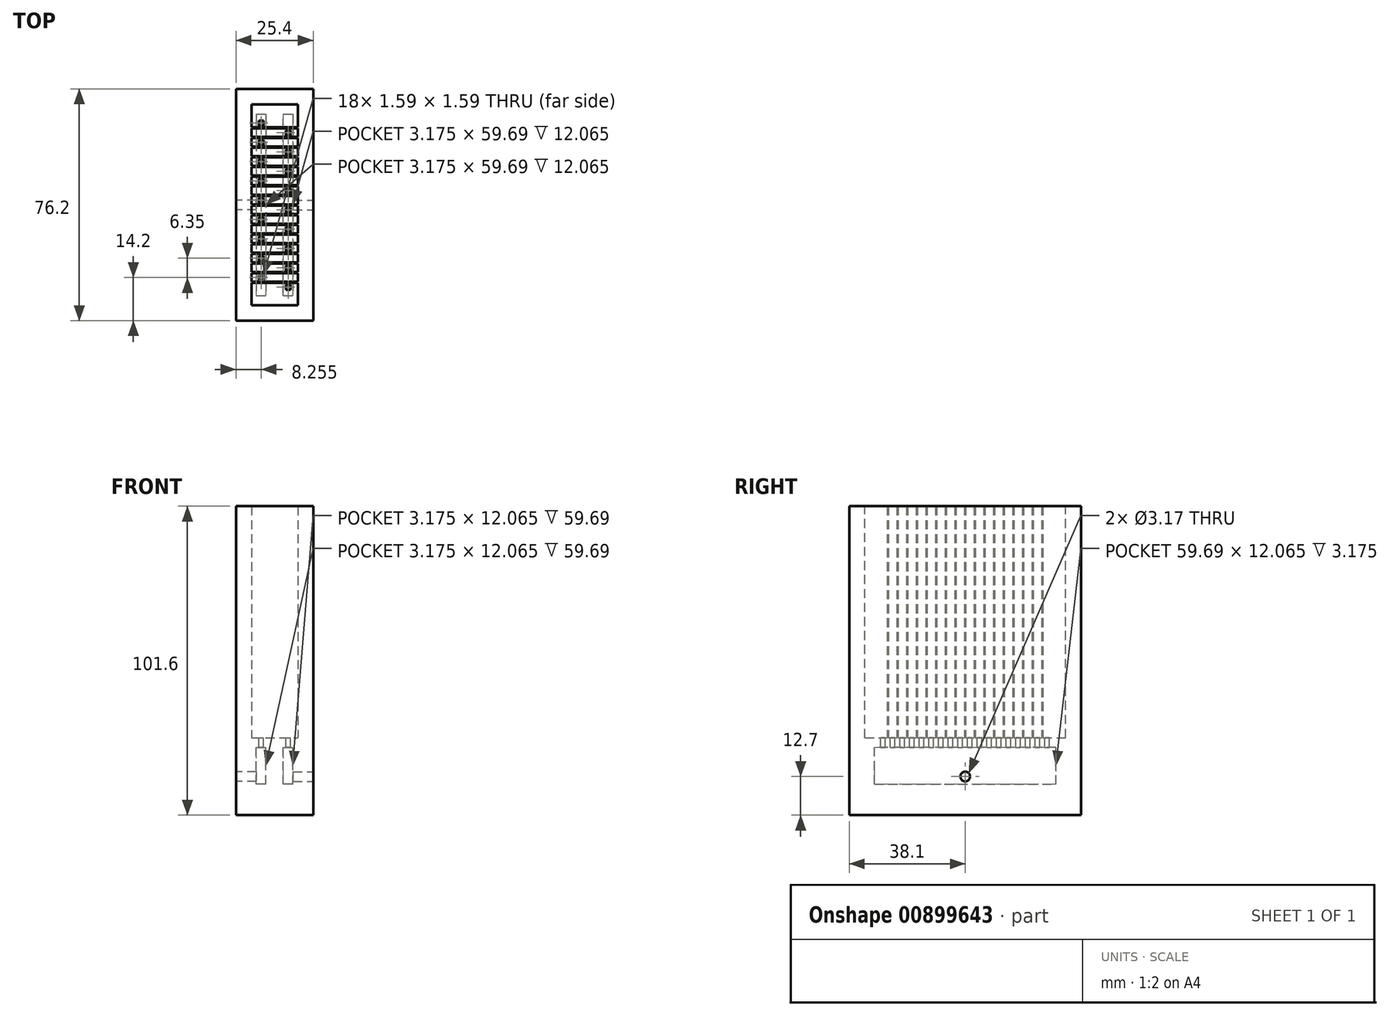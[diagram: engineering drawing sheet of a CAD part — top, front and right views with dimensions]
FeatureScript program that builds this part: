
annotation { "Feature Type Name" : "Feature", "Feature Type Description" : "" }
export const myFeature = defineFeature(function(context is Context, id is Id, definition is map)
    precondition{}
    {
        {
            var Q0;
            Q0=qCreatedBy(makeId("Top.planeOp"),FACE);
            var sketch = newSketch(context, id + "F0", { "sketchPlane" : qUnion([Q0])});
            skLineSegment(sketch, "E0.bottom", {"start": v(0, 0) * mm, "end": v(25.4, 0) * mm});
            skLineSegment(sketch, "E0.top", {"start": v(0, 76.2) * mm, "end": v(25.4, 76.2) * mm});
            skLineSegment(sketch, "E0.left", {"start": v(0, 0) * mm, "end": v(0, 76.2) * mm});
            skLineSegment(sketch, "E0.right", {"start": v(25.4, 0) * mm, "end": v(25.4, 76.2) * mm});
            skSolve(sketch);
        }
        {
            var Q0;
            Q0=makeQuery(id+"F0.imprint","IMPRINT",FACE,{"disambiguationData":[TD([[makeQuery(id+"F0.imprint","IMPRINT",EDGE,{"derivedFrom":sQuery(id+"F0.wireOp",EDGE,"E0.bottom")}),1.0]])]});
            extrude(context, id + "F1", {"entities" : qUnion([Q0]), "depth" : 101.6 * mm, "offsetDistance" : 25.4 * mm});
        }
        {
            var Q0;
            Q0=makeQuery(id+"F1.opExtrude","CAP_FACE",FACE,{"disambiguationData":[OSD([sQuery(id+"F0.wireOp",EDGE,"E0.bottom"),sQuery(id+"F0.wireOp",EDGE,"E0.top"),sQuery(id+"F0.wireOp",EDGE,"E0.left"),sQuery(id+"F0.wireOp",EDGE,"E0.right")])],"isStart":false});
            var sketch = newSketch(context, id + "F2", { "sketchPlane" : qUnion([Q0])});
            skLineSegment(sketch, "E1.bottom", {"start": v(5.08, 5.08) * mm, "end": v(20.32, 5.08) * mm});
            skLineSegment(sketch, "E1.top", {"start": v(5.08, 71.12) * mm, "end": v(20.32, 71.12) * mm});
            skLineSegment(sketch, "E1.left", {"start": v(5.08, 5.08) * mm, "end": v(5.08, 71.12) * mm});
            skLineSegment(sketch, "E1.right", {"start": v(20.32, 5.08) * mm, "end": v(20.32, 71.12) * mm});
            skSolve(sketch);
        }
        {
            var Q0;
            Q0=makeQuery(id+"F2.imprint","IMPRINT",FACE,{"disambiguationData":[TD([[makeQuery(id+"F2.imprint","IMPRINT",EDGE,{"derivedFrom":sQuery(id+"F2.wireOp",EDGE,"E1.bottom")}),1.0]])]});
            extrude(context, id + "F3", {"entities" : qUnion([Q0]), "operationType" : NewBodyOperationType.REMOVE, "oppositeDirection" : true, "depth" : 76.2 * mm, "offsetDistance" : 25.4 * mm});
        }
        {
            var Q0;
            Q0=makeQuery(id+"F1.opExtrude","SWEPT_FACE",FACE,{"disambiguationData":[OSD([sQuery(id+"F0.wireOp",EDGE,"E0.right")])]});
            var sketch = newSketch(context, id + "F4", { "sketchPlane" : qUnion([Q0])});
            skCircle(sketch, "E2", {"center": v(38.1, 12.7) * mm, "radius": 1.59 * mm});
            skSolve(sketch);
        }
        {
            var Q0;
            Q0=makeQuery(id+"F3.boolean.opBoolean","COPY",FACE,{"derivedFrom":makeQuery(id+"F3.opExtrude","CAP_FACE",FACE,{"disambiguationData":[OSD([sQuery(id+"F2.wireOp",EDGE,"E1.bottom"),sQuery(id+"F2.wireOp",EDGE,"E1.top"),sQuery(id+"F2.wireOp",EDGE,"E1.left"),sQuery(id+"F2.wireOp",EDGE,"E1.right")])],"isStart":false})});
            var sketch = newSketch(context, id + "F5", { "sketchPlane" : qUnion([Q0])});
            skLineSegment(sketch, "E3.bottom", {"start": v(15.56, 67.95) * mm, "end": v(18.73, 67.95) * mm});
            skLineSegment(sketch, "E3.top", {"start": v(15.56, 8.26) * mm, "end": v(18.73, 8.26) * mm});
            skLineSegment(sketch, "E3.left", {"start": v(15.56, 67.95) * mm, "end": v(15.56, 8.26) * mm});
            skLineSegment(sketch, "E3.right", {"start": v(18.73, 67.95) * mm, "end": v(18.73, 8.25) * mm});
            skLineSegment(sketch, "E4.bottom", {"start": v(6.67, 67.95) * mm, "end": v(9.84, 67.95) * mm});
            skLineSegment(sketch, "E4.top", {"start": v(6.67, 8.25) * mm, "end": v(9.84, 8.25) * mm});
            skLineSegment(sketch, "E4.left", {"start": v(6.67, 67.95) * mm, "end": v(6.67, 8.25) * mm});
            skLineSegment(sketch, "E4.right", {"start": v(9.84, 67.95) * mm, "end": v(9.84, 8.25) * mm});
            skSolve(sketch);
        }
        {
            var Q0;
            Q0 = qSketchRegion(id + "F5", true);
            extrude(context, id + "F6", {"entities" : qUnion([Q0]), "operationType" : NewBodyOperationType.REMOVE, "endBound" : BoundingType.UP_TO_NEXT, "oppositeDirection" : true, "depth" : 25.4 * mm, "hasOffset" : true, "offsetDistance" : 10.16 * mm, "hasSecondDirection" : true, "secondDirectionOppositeDirection" : false, "secondDirectionDepth" : -3.17 * mm});
        }
        {
            var Q0;
            Q0 = qSketchRegion(id + "F4", true);
            extrude(context, id + "F7", {"entities" : qUnion([Q0]), "operationType" : NewBodyOperationType.REMOVE, "endBound" : BoundingType.UP_TO_NEXT, "oppositeDirection" : true, "depth" : 25.4 * mm, "offsetDistance" : 25.4 * mm});
        }
        {
            var Q0;
            Q0=makeQuery(id+"F1.opExtrude","SWEPT_FACE",FACE,{"disambiguationData":[OSD([sQuery(id+"F0.wireOp",EDGE,"E0.left")])]});
            var sketch = newSketch(context, id + "F8", { "sketchPlane" : qUnion([Q0])});
            skCircle(sketch, "E5", {"center": v(-38.1, 12.7) * mm, "radius": 1.59 * mm});
            skSolve(sketch);
        }
        {
            var Q0;
            Q0 = qSketchRegion(id + "F8", true);
            extrude(context, id + "F9", {"entities" : qUnion([Q0]), "operationType" : NewBodyOperationType.REMOVE, "endBound" : BoundingType.UP_TO_NEXT, "oppositeDirection" : true, "depth" : 25.4 * mm, "offsetDistance" : 25.4 * mm});
        }
        {
            var Q0;
            Q0=makeQuery(id+"F3.boolean.opBoolean","COPY",FACE,{"derivedFrom":makeQuery(id+"F3.opExtrude","CAP_FACE",FACE,{"disambiguationData":[OSD([sQuery(id+"F2.wireOp",EDGE,"E1.bottom"),sQuery(id+"F2.wireOp",EDGE,"E1.top"),sQuery(id+"F2.wireOp",EDGE,"E1.left"),sQuery(id+"F2.wireOp",EDGE,"E1.right")])],"isStart":false})});
            var sketch = newSketch(context, id + "F10", { "sketchPlane" : qUnion([Q0])});
            skLineSegment(sketch, "E6.bottom", {"start": v(7.46, 65.8) * mm, "end": v(9.05, 65.8) * mm});
            skLineSegment(sketch, "E6.top", {"start": v(7.46, 64.2) * mm, "end": v(9.05, 64.2) * mm});
            skLineSegment(sketch, "E6.left", {"start": v(7.46, 65.8) * mm, "end": v(7.46, 64.2) * mm});
            skLineSegment(sketch, "E6.right", {"start": v(9.05, 65.8) * mm, "end": v(9.05, 64.2) * mm});
            skLineSegment(sketch, "E7.0.1.0", {"start": v(9.05, 59.44) * mm, "end": v(9.05, 57.86) * mm});
            skLineSegment(sketch, "E7.0.1.1", {"start": v(7.46, 59.44) * mm, "end": v(7.46, 57.86) * mm});
            skLineSegment(sketch, "E7.0.1.2", {"start": v(7.46, 57.86) * mm, "end": v(9.05, 57.86) * mm});
            skLineSegment(sketch, "E7.0.1.3", {"start": v(7.46, 59.44) * mm, "end": v(9.05, 59.44) * mm});
            skLineSegment(sketch, "E7.0.2.0", {"start": v(9.05, 53.1) * mm, "end": v(9.05, 51.5) * mm});
            skLineSegment(sketch, "E7.0.2.1", {"start": v(7.46, 53.1) * mm, "end": v(7.46, 51.5) * mm});
            skLineSegment(sketch, "E7.0.2.2", {"start": v(7.46, 51.5) * mm, "end": v(9.05, 51.5) * mm});
            skLineSegment(sketch, "E7.0.2.3", {"start": v(7.46, 53.1) * mm, "end": v(9.05, 53.1) * mm});
            skLineSegment(sketch, "E7.0.3.0", {"start": v(9.05, 46.74) * mm, "end": v(9.05, 45.16) * mm});
            skLineSegment(sketch, "E7.0.3.1", {"start": v(7.46, 46.74) * mm, "end": v(7.46, 45.16) * mm});
            skLineSegment(sketch, "E7.0.3.2", {"start": v(7.46, 45.16) * mm, "end": v(9.05, 45.16) * mm});
            skLineSegment(sketch, "E7.0.3.3", {"start": v(7.46, 46.74) * mm, "end": v(9.05, 46.74) * mm});
            skLineSegment(sketch, "E7.0.4.0", {"start": v(9.05, 40.4) * mm, "end": v(9.05, 38.8) * mm});
            skLineSegment(sketch, "E7.0.4.1", {"start": v(7.46, 40.4) * mm, "end": v(7.46, 38.8) * mm});
            skLineSegment(sketch, "E7.0.4.2", {"start": v(7.46, 38.8) * mm, "end": v(9.05, 38.8) * mm});
            skLineSegment(sketch, "E7.0.4.3", {"start": v(7.46, 40.4) * mm, "end": v(9.05, 40.4) * mm});
            skLineSegment(sketch, "E7.0.5.0", {"start": v(9.05, 34.04) * mm, "end": v(9.05, 32.46) * mm});
            skLineSegment(sketch, "E7.0.5.1", {"start": v(7.46, 34.04) * mm, "end": v(7.46, 32.46) * mm});
            skLineSegment(sketch, "E7.0.5.2", {"start": v(7.46, 32.46) * mm, "end": v(9.05, 32.46) * mm});
            skLineSegment(sketch, "E7.0.5.3", {"start": v(7.46, 34.04) * mm, "end": v(9.05, 34.04) * mm});
            skLineSegment(sketch, "E7.0.6.0", {"start": v(9.05, 27.7) * mm, "end": v(9.05, 26.1) * mm});
            skLineSegment(sketch, "E7.0.6.1", {"start": v(7.46, 27.7) * mm, "end": v(7.46, 26.1) * mm});
            skLineSegment(sketch, "E7.0.6.2", {"start": v(7.46, 26.1) * mm, "end": v(9.05, 26.1) * mm});
            skLineSegment(sketch, "E7.0.6.3", {"start": v(7.46, 27.7) * mm, "end": v(9.05, 27.7) * mm});
            skLineSegment(sketch, "E7.0.7.0", {"start": v(9.05, 21.34) * mm, "end": v(9.05, 19.76) * mm});
            skLineSegment(sketch, "E7.0.7.1", {"start": v(7.46, 21.34) * mm, "end": v(7.46, 19.76) * mm});
            skLineSegment(sketch, "E7.0.7.2", {"start": v(7.46, 19.76) * mm, "end": v(9.05, 19.76) * mm});
            skLineSegment(sketch, "E7.0.7.3", {"start": v(7.46, 21.34) * mm, "end": v(9.05, 21.34) * mm});
            skLineSegment(sketch, "E7.0.8.0", {"start": v(9.05, 15) * mm, "end": v(9.05, 13.4) * mm});
            skLineSegment(sketch, "E7.0.8.1", {"start": v(7.46, 15) * mm, "end": v(7.46, 13.4) * mm});
            skLineSegment(sketch, "E7.0.8.2", {"start": v(7.46, 13.4) * mm, "end": v(9.05, 13.4) * mm});
            skLineSegment(sketch, "E7.0.8.3", {"start": v(7.46, 15) * mm, "end": v(9.05, 15) * mm});
            skLineSegment(sketch, "E7.direction1", {"start": v(7.46, 64.2) * mm, "end": v(46.74, 64) * mm, "construction": true});
            skLineSegment(sketch, "E7.direction2", {"start": v(7.46, 64.2) * mm, "end": v(7.46, 57.86) * mm, "construction": true});
            skSolve(sketch);
        }
        {
            var Q0;
            Q0 = qSketchRegion(id + "F10", true);
            extrude(context, id + "F11", {"entities" : qUnion([Q0]), "operationType" : NewBodyOperationType.REMOVE, "endBound" : BoundingType.UP_TO_NEXT, "oppositeDirection" : true, "depth" : 25.4 * mm, "offsetDistance" : 25.4 * mm});
        }
        {
            var Q0;
            Q0=makeQuery(id+"F3.boolean.opBoolean","COPY",FACE,{"derivedFrom":makeQuery(id+"F3.opExtrude","CAP_FACE",FACE,{"disambiguationData":[OSD([sQuery(id+"F2.wireOp",EDGE,"E1.bottom"),sQuery(id+"F2.wireOp",EDGE,"E1.top"),sQuery(id+"F2.wireOp",EDGE,"E1.left"),sQuery(id+"F2.wireOp",EDGE,"E1.right")])],"isStart":false})});
            var sketch = newSketch(context, id + "F12", { "sketchPlane" : qUnion([Q0])});
            skLineSegment(sketch, "E8.bottom", {"start": v(16.35, 62.62) * mm, "end": v(17.94, 62.62) * mm});
            skLineSegment(sketch, "E8.top", {"start": v(16.35, 61.03) * mm, "end": v(17.94, 61.03) * mm});
            skLineSegment(sketch, "E8.left", {"start": v(16.35, 62.62) * mm, "end": v(16.35, 61.03) * mm});
            skLineSegment(sketch, "E8.right", {"start": v(17.94, 62.62) * mm, "end": v(17.94, 61.03) * mm});
            skLineSegment(sketch, "E9.0.1.0", {"start": v(16.35, 56.27) * mm, "end": v(16.35, 54.68) * mm});
            skLineSegment(sketch, "E9.0.1.1", {"start": v(16.35, 54.68) * mm, "end": v(17.94, 54.68) * mm});
            skLineSegment(sketch, "E9.0.1.2", {"start": v(16.35, 56.27) * mm, "end": v(17.94, 56.27) * mm});
            skLineSegment(sketch, "E9.0.1.3", {"start": v(17.94, 56.27) * mm, "end": v(17.94, 54.68) * mm});
            skLineSegment(sketch, "E9.0.2.0", {"start": v(16.35, 49.92) * mm, "end": v(16.35, 48.33) * mm});
            skLineSegment(sketch, "E9.0.2.1", {"start": v(16.35, 48.33) * mm, "end": v(17.94, 48.33) * mm});
            skLineSegment(sketch, "E9.0.2.2", {"start": v(16.35, 49.92) * mm, "end": v(17.94, 49.92) * mm});
            skLineSegment(sketch, "E9.0.2.3", {"start": v(17.94, 49.92) * mm, "end": v(17.94, 48.33) * mm});
            skLineSegment(sketch, "E9.0.3.0", {"start": v(16.35, 43.57) * mm, "end": v(16.35, 41.98) * mm});
            skLineSegment(sketch, "E9.0.3.1", {"start": v(16.35, 41.98) * mm, "end": v(17.94, 41.98) * mm});
            skLineSegment(sketch, "E9.0.3.2", {"start": v(16.35, 43.57) * mm, "end": v(17.94, 43.57) * mm});
            skLineSegment(sketch, "E9.0.3.3", {"start": v(17.94, 43.57) * mm, "end": v(17.94, 41.98) * mm});
            skLineSegment(sketch, "E9.0.4.0", {"start": v(16.35, 37.22) * mm, "end": v(16.35, 35.63) * mm});
            skLineSegment(sketch, "E9.0.4.1", {"start": v(16.35, 35.63) * mm, "end": v(17.94, 35.63) * mm});
            skLineSegment(sketch, "E9.0.4.2", {"start": v(16.35, 37.22) * mm, "end": v(17.94, 37.22) * mm});
            skLineSegment(sketch, "E9.0.4.3", {"start": v(17.94, 37.22) * mm, "end": v(17.94, 35.63) * mm});
            skLineSegment(sketch, "E9.0.5.0", {"start": v(16.35, 30.87) * mm, "end": v(16.35, 29.28) * mm});
            skLineSegment(sketch, "E9.0.5.1", {"start": v(16.35, 29.28) * mm, "end": v(17.94, 29.28) * mm});
            skLineSegment(sketch, "E9.0.5.2", {"start": v(16.35, 30.87) * mm, "end": v(17.94, 30.87) * mm});
            skLineSegment(sketch, "E9.0.5.3", {"start": v(17.94, 30.87) * mm, "end": v(17.94, 29.28) * mm});
            skLineSegment(sketch, "E9.0.6.0", {"start": v(16.35, 24.52) * mm, "end": v(16.35, 22.93) * mm});
            skLineSegment(sketch, "E9.0.6.1", {"start": v(16.35, 22.93) * mm, "end": v(17.94, 22.93) * mm});
            skLineSegment(sketch, "E9.0.6.2", {"start": v(16.35, 24.52) * mm, "end": v(17.94, 24.52) * mm});
            skLineSegment(sketch, "E9.0.6.3", {"start": v(17.94, 24.52) * mm, "end": v(17.94, 22.93) * mm});
            skLineSegment(sketch, "E9.0.7.0", {"start": v(16.35, 18.17) * mm, "end": v(16.35, 16.58) * mm});
            skLineSegment(sketch, "E9.0.7.1", {"start": v(16.35, 16.58) * mm, "end": v(17.94, 16.58) * mm});
            skLineSegment(sketch, "E9.0.7.2", {"start": v(16.35, 18.17) * mm, "end": v(17.94, 18.17) * mm});
            skLineSegment(sketch, "E9.0.7.3", {"start": v(17.94, 18.17) * mm, "end": v(17.94, 16.58) * mm});
            skLineSegment(sketch, "E9.0.8.0", {"start": v(16.35, 11.82) * mm, "end": v(16.35, 10.23) * mm});
            skLineSegment(sketch, "E9.0.8.1", {"start": v(16.35, 10.23) * mm, "end": v(17.94, 10.23) * mm});
            skLineSegment(sketch, "E9.0.8.2", {"start": v(16.35, 11.82) * mm, "end": v(17.94, 11.82) * mm});
            skLineSegment(sketch, "E9.0.8.3", {"start": v(17.94, 11.82) * mm, "end": v(17.94, 10.23) * mm});
            skLineSegment(sketch, "E9.direction1", {"start": v(16.35, 61.03) * mm, "end": v(41.75, 61.03) * mm, "construction": true});
            skLineSegment(sketch, "E9.direction2", {"start": v(16.35, 61.03) * mm, "end": v(16.35, 54.68) * mm, "construction": true});
            skSolve(sketch);
        }
        {
            var Q0;
            Q0 = qSketchRegion(id + "F12", true);
            extrude(context, id + "F13", {"entities" : qUnion([Q0]), "operationType" : NewBodyOperationType.REMOVE, "endBound" : BoundingType.UP_TO_NEXT, "oppositeDirection" : true, "depth" : 25.4 * mm, "offsetDistance" : 25.4 * mm});
        }
        {
            var Q0;
            Q0=makeQuery(id+"F3.boolean.opBoolean","COPY",FACE,{"derivedFrom":makeQuery(id+"F3.opExtrude","CAP_FACE",FACE,{"disambiguationData":[OSD([sQuery(id+"F2.wireOp",EDGE,"E1.bottom"),sQuery(id+"F2.wireOp",EDGE,"E1.top"),sQuery(id+"F2.wireOp",EDGE,"E1.left"),sQuery(id+"F2.wireOp",EDGE,"E1.right")])],"isStart":false})});
            var sketch = newSketch(context, id + "F14", { "sketchPlane" : qUnion([Q0])});
            skLineSegment(sketch, "E10.bottom", {"start": v(5.08, 63.61) * mm, "end": v(20.32, 63.61) * mm});
            skLineSegment(sketch, "E10.top", {"start": v(5.08, 63.21) * mm, "end": v(20.32, 63.21) * mm});
            skLineSegment(sketch, "E10.left", {"start": v(5.08, 63.61) * mm, "end": v(5.08, 63.21) * mm});
            skLineSegment(sketch, "E10.right", {"start": v(20.32, 63.61) * mm, "end": v(20.32, 63.21) * mm});
            skLineSegment(sketch, "E11.0.1.0", {"start": v(5.08, 60.44) * mm, "end": v(20.32, 60.44) * mm});
            skLineSegment(sketch, "E11.0.1.1", {"start": v(5.08, 60.04) * mm, "end": v(20.32, 60.04) * mm});
            skLineSegment(sketch, "E11.0.1.2", {"start": v(5.08, 60.44) * mm, "end": v(5.08, 60.04) * mm});
            skLineSegment(sketch, "E11.0.1.3", {"start": v(20.32, 60.44) * mm, "end": v(20.32, 60.04) * mm});
            skLineSegment(sketch, "E11.0.2.0", {"start": v(5.08, 57.26) * mm, "end": v(20.32, 57.26) * mm});
            skLineSegment(sketch, "E11.0.2.1", {"start": v(5.08, 56.86) * mm, "end": v(20.32, 56.86) * mm});
            skLineSegment(sketch, "E11.0.2.2", {"start": v(5.08, 57.26) * mm, "end": v(5.08, 56.86) * mm});
            skLineSegment(sketch, "E11.0.2.3", {"start": v(20.32, 57.26) * mm, "end": v(20.32, 56.86) * mm});
            skLineSegment(sketch, "E11.0.3.0", {"start": v(5.08, 54.09) * mm, "end": v(20.32, 54.09) * mm});
            skLineSegment(sketch, "E11.0.3.1", {"start": v(5.08, 53.69) * mm, "end": v(20.32, 53.69) * mm});
            skLineSegment(sketch, "E11.0.3.2", {"start": v(5.08, 54.09) * mm, "end": v(5.08, 53.69) * mm});
            skLineSegment(sketch, "E11.0.3.3", {"start": v(20.32, 54.09) * mm, "end": v(20.32, 53.69) * mm});
            skLineSegment(sketch, "E11.0.4.0", {"start": v(5.08, 50.91) * mm, "end": v(20.32, 50.91) * mm});
            skLineSegment(sketch, "E11.0.4.1", {"start": v(5.08, 50.51) * mm, "end": v(20.32, 50.51) * mm});
            skLineSegment(sketch, "E11.0.4.2", {"start": v(5.08, 50.91) * mm, "end": v(5.08, 50.51) * mm});
            skLineSegment(sketch, "E11.0.4.3", {"start": v(20.32, 50.91) * mm, "end": v(20.32, 50.51) * mm});
            skLineSegment(sketch, "E11.0.5.0", {"start": v(5.08, 47.74) * mm, "end": v(20.32, 47.74) * mm});
            skLineSegment(sketch, "E11.0.5.1", {"start": v(5.08, 47.34) * mm, "end": v(20.32, 47.34) * mm});
            skLineSegment(sketch, "E11.0.5.2", {"start": v(5.08, 47.74) * mm, "end": v(5.08, 47.34) * mm});
            skLineSegment(sketch, "E11.0.5.3", {"start": v(20.32, 47.74) * mm, "end": v(20.32, 47.34) * mm});
            skLineSegment(sketch, "E11.0.6.0", {"start": v(5.08, 44.56) * mm, "end": v(20.32, 44.56) * mm});
            skLineSegment(sketch, "E11.0.6.1", {"start": v(5.08, 44.16) * mm, "end": v(20.32, 44.16) * mm});
            skLineSegment(sketch, "E11.0.6.2", {"start": v(5.08, 44.56) * mm, "end": v(5.08, 44.16) * mm});
            skLineSegment(sketch, "E11.0.6.3", {"start": v(20.32, 44.56) * mm, "end": v(20.32, 44.16) * mm});
            skLineSegment(sketch, "E11.0.7.0", {"start": v(5.08, 41.39) * mm, "end": v(20.32, 41.39) * mm});
            skLineSegment(sketch, "E11.0.7.1", {"start": v(5.08, 40.99) * mm, "end": v(20.32, 40.99) * mm});
            skLineSegment(sketch, "E11.0.7.2", {"start": v(5.08, 41.39) * mm, "end": v(5.08, 40.99) * mm});
            skLineSegment(sketch, "E11.0.7.3", {"start": v(20.32, 41.39) * mm, "end": v(20.32, 40.99) * mm});
            skLineSegment(sketch, "E11.0.8.0", {"start": v(5.08, 38.21) * mm, "end": v(20.32, 38.21) * mm});
            skLineSegment(sketch, "E11.0.8.1", {"start": v(5.08, 37.81) * mm, "end": v(20.32, 37.81) * mm});
            skLineSegment(sketch, "E11.0.8.2", {"start": v(5.08, 38.21) * mm, "end": v(5.08, 37.81) * mm});
            skLineSegment(sketch, "E11.0.8.3", {"start": v(20.32, 38.21) * mm, "end": v(20.32, 37.81) * mm});
            skLineSegment(sketch, "E11.0.9.0", {"start": v(5.08, 35.04) * mm, "end": v(20.32, 35.04) * mm});
            skLineSegment(sketch, "E11.0.9.1", {"start": v(5.08, 34.64) * mm, "end": v(20.32, 34.64) * mm});
            skLineSegment(sketch, "E11.0.9.2", {"start": v(5.08, 35.04) * mm, "end": v(5.08, 34.64) * mm});
            skLineSegment(sketch, "E11.0.9.3", {"start": v(20.32, 35.04) * mm, "end": v(20.32, 34.64) * mm});
            skLineSegment(sketch, "E11.0.10.0", {"start": v(5.08, 31.86) * mm, "end": v(20.32, 31.86) * mm});
            skLineSegment(sketch, "E11.0.10.1", {"start": v(5.08, 31.46) * mm, "end": v(20.32, 31.46) * mm});
            skLineSegment(sketch, "E11.0.10.2", {"start": v(5.08, 31.86) * mm, "end": v(5.08, 31.46) * mm});
            skLineSegment(sketch, "E11.0.10.3", {"start": v(20.32, 31.86) * mm, "end": v(20.32, 31.46) * mm});
            skLineSegment(sketch, "E11.0.11.0", {"start": v(5.08, 28.69) * mm, "end": v(20.32, 28.69) * mm});
            skLineSegment(sketch, "E11.0.11.1", {"start": v(5.08, 28.29) * mm, "end": v(20.32, 28.29) * mm});
            skLineSegment(sketch, "E11.0.11.2", {"start": v(5.08, 28.69) * mm, "end": v(5.08, 28.29) * mm});
            skLineSegment(sketch, "E11.0.11.3", {"start": v(20.32, 28.69) * mm, "end": v(20.32, 28.29) * mm});
            skLineSegment(sketch, "E11.0.12.0", {"start": v(5.08, 25.51) * mm, "end": v(20.32, 25.51) * mm});
            skLineSegment(sketch, "E11.0.12.1", {"start": v(5.08, 25.11) * mm, "end": v(20.32, 25.11) * mm});
            skLineSegment(sketch, "E11.0.12.2", {"start": v(5.08, 25.51) * mm, "end": v(5.08, 25.11) * mm});
            skLineSegment(sketch, "E11.0.12.3", {"start": v(20.32, 25.51) * mm, "end": v(20.32, 25.11) * mm});
            skLineSegment(sketch, "E11.0.13.0", {"start": v(5.08, 22.34) * mm, "end": v(20.32, 22.34) * mm});
            skLineSegment(sketch, "E11.0.13.1", {"start": v(5.08, 21.94) * mm, "end": v(20.32, 21.94) * mm});
            skLineSegment(sketch, "E11.0.13.2", {"start": v(5.08, 22.34) * mm, "end": v(5.08, 21.94) * mm});
            skLineSegment(sketch, "E11.0.13.3", {"start": v(20.32, 22.34) * mm, "end": v(20.32, 21.94) * mm});
            skLineSegment(sketch, "E11.0.14.0", {"start": v(5.08, 19.16) * mm, "end": v(20.32, 19.16) * mm});
            skLineSegment(sketch, "E11.0.14.1", {"start": v(5.08, 18.76) * mm, "end": v(20.32, 18.76) * mm});
            skLineSegment(sketch, "E11.0.14.2", {"start": v(5.08, 19.16) * mm, "end": v(5.08, 18.76) * mm});
            skLineSegment(sketch, "E11.0.14.3", {"start": v(20.32, 19.16) * mm, "end": v(20.32, 18.76) * mm});
            skLineSegment(sketch, "E11.0.15.0", {"start": v(5.08, 15.99) * mm, "end": v(20.32, 15.99) * mm});
            skLineSegment(sketch, "E11.0.15.1", {"start": v(5.08, 15.59) * mm, "end": v(20.32, 15.59) * mm});
            skLineSegment(sketch, "E11.0.15.2", {"start": v(5.08, 15.99) * mm, "end": v(5.08, 15.59) * mm});
            skLineSegment(sketch, "E11.0.15.3", {"start": v(20.32, 15.99) * mm, "end": v(20.32, 15.59) * mm});
            skLineSegment(sketch, "E11.0.16.0", {"start": v(5.08, 12.81) * mm, "end": v(20.32, 12.81) * mm});
            skLineSegment(sketch, "E11.0.16.1", {"start": v(5.08, 12.41) * mm, "end": v(20.32, 12.41) * mm});
            skLineSegment(sketch, "E11.0.16.2", {"start": v(5.08, 12.81) * mm, "end": v(5.08, 12.41) * mm});
            skLineSegment(sketch, "E11.0.16.3", {"start": v(20.32, 12.81) * mm, "end": v(20.32, 12.41) * mm});
            skLineSegment(sketch, "E11.direction1", {"start": v(5.08, 63.21) * mm, "end": v(30.48, 63.21) * mm, "construction": true});
            skLineSegment(sketch, "E11.direction2", {"start": v(5.08, 63.21) * mm, "end": v(5.08, 60.04) * mm, "construction": true});
            skSolve(sketch);
        }
        {
            var Q0;
            Q0 = qSketchRegion(id + "F14", true);
            var Q1;
            Q1=makeQuery(id+"F1.opExtrude","CAP_FACE",FACE,{"disambiguationData":[OSD([sQuery(id+"F0.wireOp",EDGE,"E0.bottom"),sQuery(id+"F0.wireOp",EDGE,"E0.top"),sQuery(id+"F0.wireOp",EDGE,"E0.left"),sQuery(id+"F0.wireOp",EDGE,"E0.right")])],"isStart":false});
            extrude(context, id + "F15", {"entities" : qUnion([Q0]), "operationType" : NewBodyOperationType.ADD, "endBound" : BoundingType.UP_TO_SURFACE, "depth" : 25.4 * mm, "endBoundEntityFace" : qUnion([Q1]), "offsetDistance" : 25.4 * mm});
        }
    });
